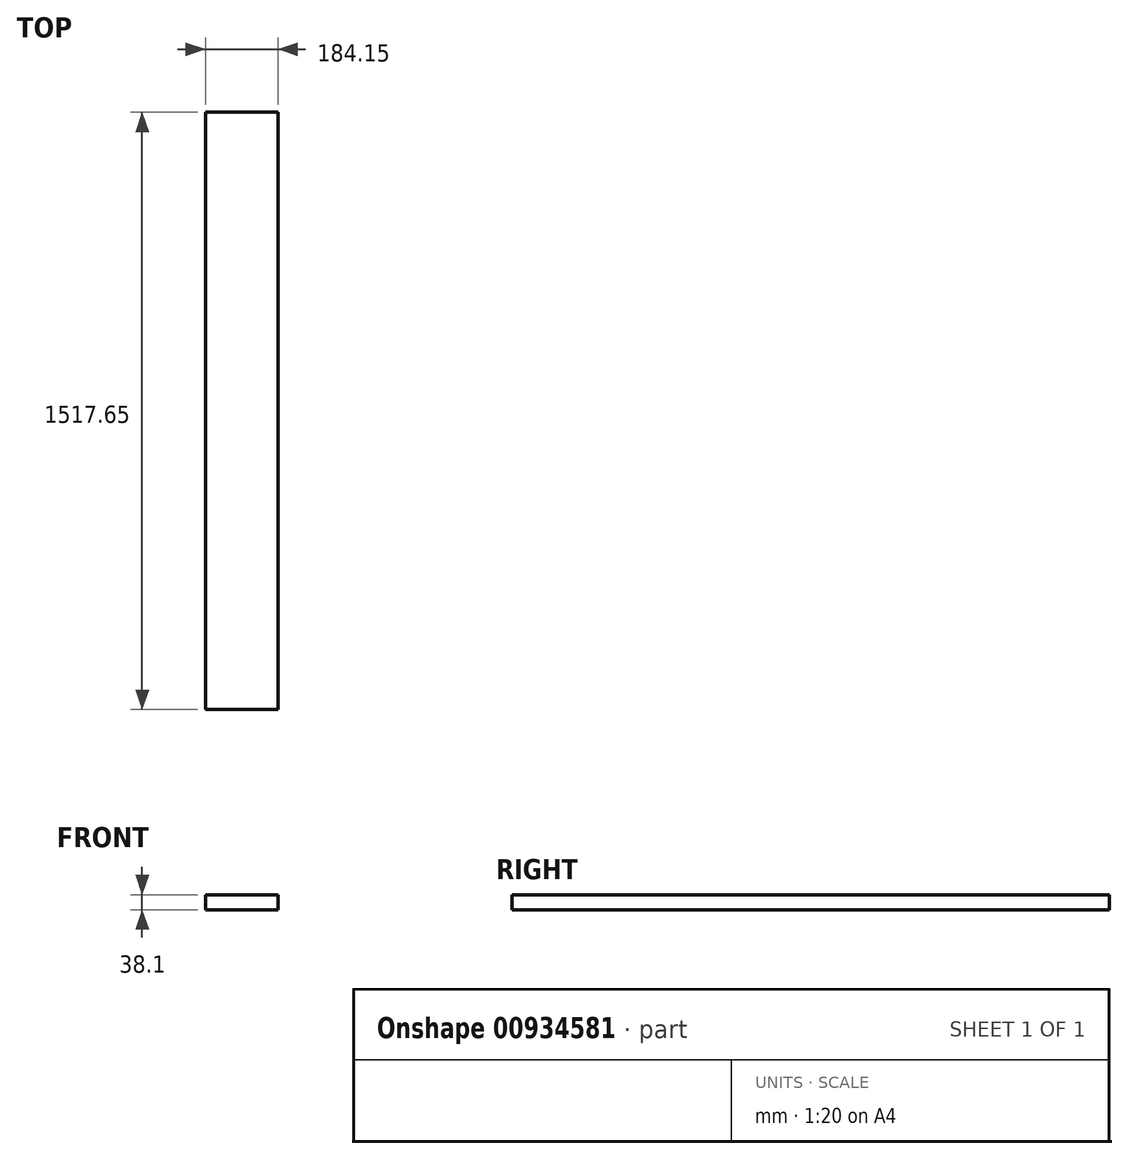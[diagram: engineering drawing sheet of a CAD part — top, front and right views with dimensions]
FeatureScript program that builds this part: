
annotation { "Feature Type Name" : "Feature", "Feature Type Description" : "" }
export const myFeature = defineFeature(function(context is Context, id is Id, definition is map)
    precondition{}
    {
        {
            var Q0;
            Q0=qCreatedBy(makeId("Front.planeOp"),FACE);
            var sketch = newSketch(context, id + "F0", { "sketchPlane" : qUnion([Q0])});
            skLineSegment(sketch, "E0.bottom", {"start": v(5223.67, -1104.19) * mm, "end": v(5407.82, -1104.19) * mm});
            skLineSegment(sketch, "E0.top", {"start": v(5223.67, -1066.09) * mm, "end": v(5407.82, -1066.09) * mm});
            skLineSegment(sketch, "E0.left", {"start": v(5223.67, -1104.19) * mm, "end": v(5223.67, -1066.09) * mm});
            skLineSegment(sketch, "E0.right", {"start": v(5407.82, -1104.19) * mm, "end": v(5407.82, -1066.09) * mm});
            skSolve(sketch);
        }
        {
            var Q0;
            Q0=makeQuery(id+"F0.imprint","IMPRINT",FACE,{"disambiguationData":[TD([[makeQuery(id+"F0.imprint","IMPRINT",EDGE,{"derivedFrom":sQuery(id+"F0.wireOp",EDGE,"E0.bottom")}),1.0]])]});
            extrude(context, id + "F1", {"entities" : qUnion([Q0]), "depth" : 1517.65 * mm, "offsetDistance" : 25.4 * mm});
        }
    });
